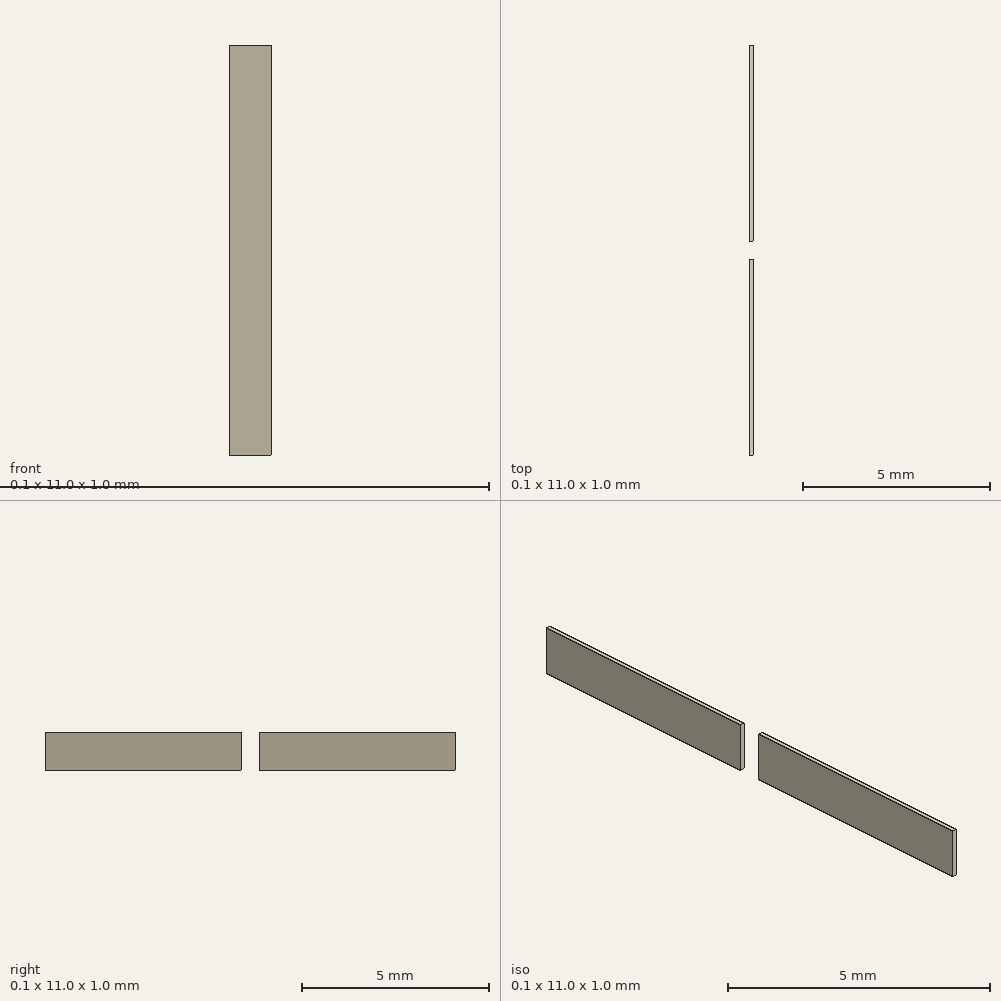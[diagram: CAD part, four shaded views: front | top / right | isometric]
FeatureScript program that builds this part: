
annotation { "Feature Type Name" : "Feature", "Feature Type Description" : "" }
export const myFeature = defineFeature(function(context is Context, id is Id, definition is map)
    precondition{}
    {
        {
            var Q0;
            Q0=qCreatedBy(makeId("Right.planeOp"),FACE);
            var sketch = newSketch(context, id + "F0", { "sketchPlane" : qUnion([Q0])});
            skPoint(sketch, "E0.0", {"position": v(0, 0) * mm});
            skLineSegment(sketch, "E1.bottom", {"start": v(0, 0) * mm, "end": v(11.5, 0) * mm});
            skLineSegment(sketch, "E1.top", {"start": v(0, -11.5) * mm, "end": v(11.5, -11.5) * mm});
            skLineSegment(sketch, "E1.left", {"start": v(0, 0) * mm, "end": v(0, -11.5) * mm});
            skLineSegment(sketch, "E1.right", {"start": v(11.5, 0) * mm, "end": v(11.5, -11.5) * mm});
            skLineSegment(sketch, "E2.0", {"start": v(5.5, -4.75) * mm, "end": v(0.25, -4.75) * mm});
            skLineSegment(sketch, "E3", {"start": v(5.5, -4.75) * mm, "end": v(5.5, -5.75) * mm});
            skLineSegment(sketch, "E4", {"start": v(5.5, -5.75) * mm, "end": v(0.25, -5.75) * mm});
            skPoint(sketch, "E5.MirrorP", {"position": v(11.5, 0) * mm});
            skLineSegment(sketch, "E6.MirrorCS", {"start": v(6, -4.75) * mm, "end": v(6, -5.75) * mm});
            skLineSegment(sketch, "E7.MirrorCS", {"start": v(6, -5.75) * mm, "end": v(11.25, -5.75) * mm});
            skLineSegment(sketch, "E8.MirrorCS", {"start": v(6, -4.75) * mm, "end": v(11.25, -4.75) * mm});
            skPoint(sketch, "E9.orphan", {"position": v(11.5, -10.25) * mm});
            skPoint(sketch, "E10.orphan", {"position": v(0, -10.25) * mm});
            skLineSegment(sketch, "E11.trimOffspring", {"start": v(11.25, -4.75) * mm, "end": v(11.25, -5.75) * mm});
            skLineSegment(sketch, "E12.trimOffspring", {"start": v(0.25, -4.75) * mm, "end": v(0.25, -5.75) * mm});
            skSolve(sketch);
        }
        {
            var Q0;
            Q0=makeQuery(id+"F0.imprint","IMPRINT",FACE,{"disambiguationData":[TD([[makeQuery(id+"F0.imprint","IMPRINT",EDGE,{"derivedFrom":sQuery(id+"F0.wireOp",EDGE,"14657d91-79c0-4d6f-9dc8-bfef05761bba.0")}),1.0]])]});
            var Q1;
            Q1=makeQuery(id+"F0.imprint","IMPRINT",FACE,{"disambiguationData":[TD([[makeQuery(id+"F0.imprint","IMPRINT",EDGE,{"derivedFrom":sQuery(id+"F0.wireOp",EDGE,"d10a1318-4c6c-4e2f-b301-627ccdfaac9c.0")}),1.0]])]});
            var Q2;
            Q2=makeQuery(id+"F0.imprint","IMPRINT",FACE,{"disambiguationData":[TD([[makeQuery(id+"F0.imprint","IMPRINT",EDGE,{"derivedFrom":sQuery(id+"F0.wireOp",EDGE,"34b941e1-9213-4a0b-9b3c-3fd5b53a19226.MirrorCS")}),1.0]])]});
            var Q3;
            Q3=makeQuery(id+"F0.imprint","IMPRINT",FACE,{"disambiguationData":[TD([[makeQuery(id+"F0.imprint","IMPRINT",EDGE,{"derivedFrom":sQuery(id+"F0.wireOp",EDGE,"e52c6cc0-2e10-4916-a505-43da0128bf07.0")}),-1.0]])]});
            var Q4;
            Q4=makeQuery(id+"F0.imprint","IMPRINT",FACE,{"disambiguationData":[TD([[makeQuery(id+"F0.imprint","IMPRINT",EDGE,{"derivedFrom":sQuery(id+"F0.wireOp",EDGE,"34b941e1-9213-4a0b-9b3c-3fd5b53a19229.MirrorCS")}),1.0]])]});
            var Q5;
            Q5=makeQuery(id+"F0.imprint","IMPRINT",FACE,{"disambiguationData":[TD([[makeQuery(id+"F0.imprint","IMPRINT",EDGE,{"derivedFrom":sQuery(id+"F0.wireOp",EDGE,"34b941e1-9213-4a0b-9b3c-3fd5b53a19223.MirrorCS")}),1.0]])]});
            var Q6;
            Q6=makeQuery(id+"F0.imprint","IMPRINT",FACE,{"disambiguationData":[TD([[makeQuery(id+"F0.imprint","IMPRINT",EDGE,{"derivedFrom":sQuery(id+"F0.wireOp",EDGE,"d212bab6-9418-4dd8-9137-893080857c44.1")}),-1.0]])]});
            var Q7;
            Q7=makeQuery(id+"F0.imprint","IMPRINT",FACE,{"disambiguationData":[TD([[makeQuery(id+"F0.imprint","IMPRINT",EDGE,{"derivedFrom":sQuery(id+"F0.wireOp",EDGE,"E6.MirrorCS")}),1.0]])]});
            var Q8;
            Q8=makeQuery(id+"F0.imprint","IMPRINT",FACE,{"disambiguationData":[TD([[makeQuery(id+"F0.imprint","IMPRINT",EDGE,{"derivedFrom":sQuery(id+"F0.wireOp",EDGE,"34b941e1-9213-4a0b-9b3c-3fd5b53a19224.MirrorCS")}),1.0]])]});
            var Q9;
            Q9=makeQuery(id+"F0.imprint","IMPRINT",FACE,{"disambiguationData":[TD([[makeQuery(id+"F0.imprint","IMPRINT",EDGE,{"derivedFrom":sQuery(id+"F0.wireOp",EDGE,"34b941e1-9213-4a0b-9b3c-3fd5b53a19221.MirrorCS")}),-1.0]])]});
            var Q10;
            Q10=makeQuery(id+"F0.imprint","IMPRINT",FACE,{"disambiguationData":[TD([[makeQuery(id+"F0.imprint","IMPRINT",EDGE,{"derivedFrom":sQuery(id+"F0.wireOp",EDGE,"E2.0")}),1.0]])]});
            var Q11;
            Q11=makeQuery(id+"F0.imprint","IMPRINT",FACE,{"disambiguationData":[TD([[makeQuery(id+"F0.imprint","IMPRINT",EDGE,{"derivedFrom":sQuery(id+"F0.wireOp",EDGE,"7881708b-2482-4012-b24c-5590632c987f.0")}),1.0]])]});
            var Q12;
            Q12=makeQuery(id+"F0.imprint","IMPRINT",FACE,{"disambiguationData":[TD([[makeQuery(id+"F0.imprint","IMPRINT",EDGE,{"derivedFrom":sQuery(id+"F0.wireOp",EDGE,"b2c296a6-979c-4eb4-8951-c574cebceffd.0")}),1.0]])]});
            var Q13;
            Q13=makeQuery(id+"F0.imprint","IMPRINT",FACE,{"disambiguationData":[TD([[makeQuery(id+"F0.imprint","IMPRINT",EDGE,{"derivedFrom":sQuery(id+"F0.wireOp",EDGE,"d212bab6-9418-4dd8-9137-893080857c44.0")}),-1.0]])]});
            extrude(context, id + "F1", {"entities" : qUnion([Q0, Q1, Q2, Q3, Q4, Q5, Q6, Q7, Q8, Q9, Q10, Q11, Q12, Q13]), "depth" : .1 * mm, "offsetDistance" : 25 * mm});
        }
    });
